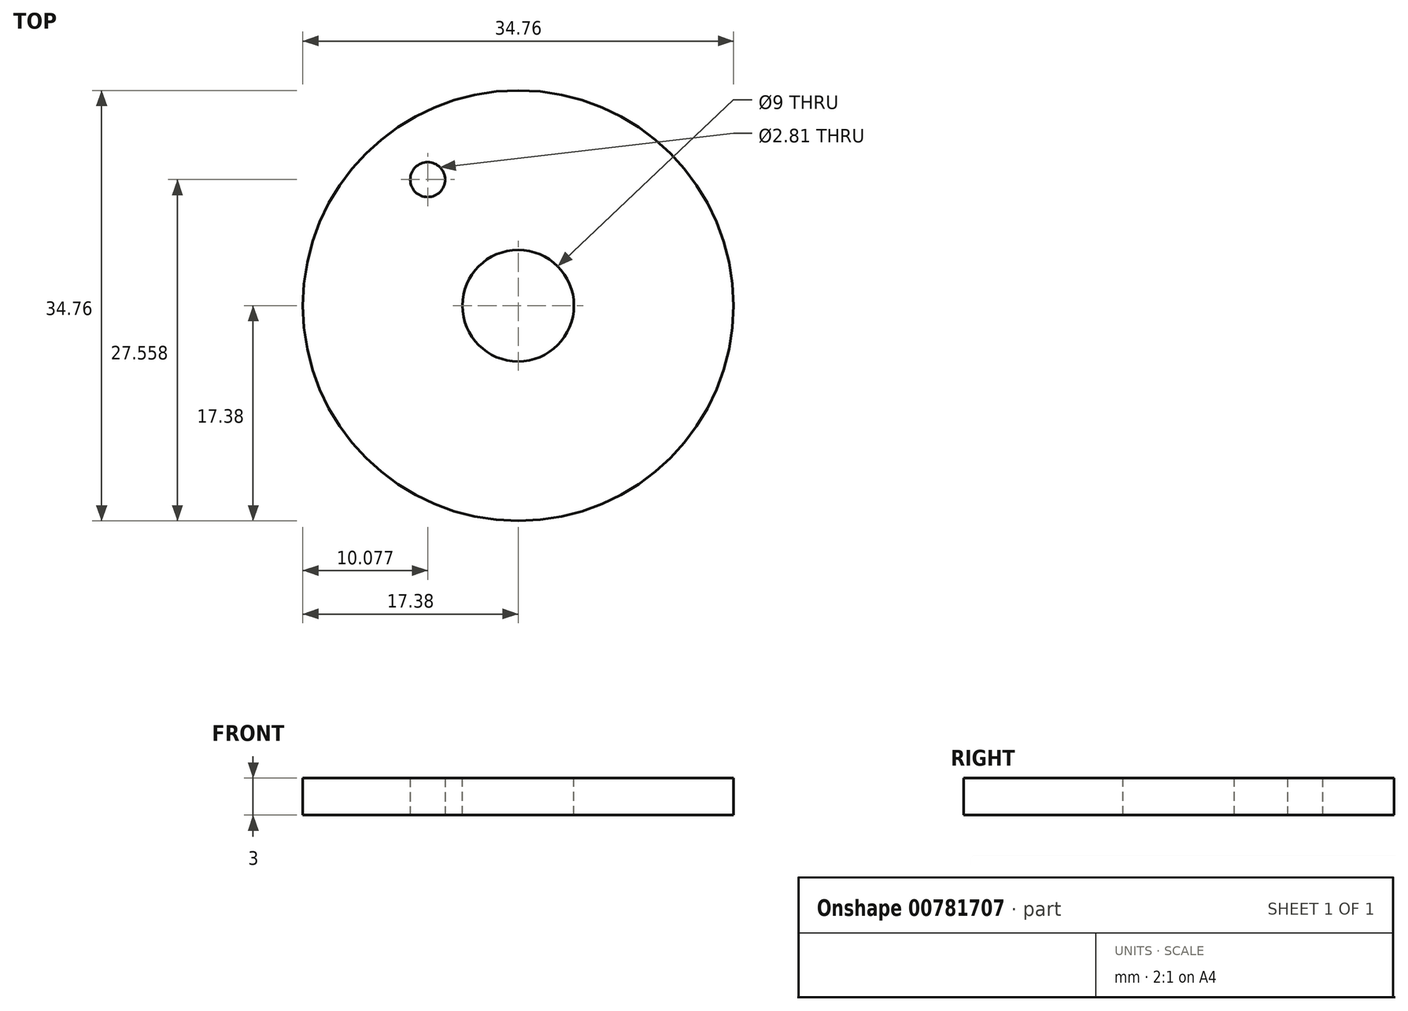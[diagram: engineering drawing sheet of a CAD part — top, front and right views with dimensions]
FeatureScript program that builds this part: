
annotation { "Feature Type Name" : "Feature", "Feature Type Description" : "" }
export const myFeature = defineFeature(function(context is Context, id is Id, definition is map)
    precondition{}
    {
        {
            var Q0;
            Q0=qCreatedBy(makeId("Top.planeOp"),FACE);
            var sketch = newSketch(context, id + "F0", { "sketchPlane" : qUnion([Q0])});
            skCircle(sketch, "E0", {"center": v(0, 0) * mm, "radius": 17.38 * mm});
            skSolve(sketch);
        }
        {
            var Q0;
            Q0=makeQuery(id+"F0.imprint","IMPRINT",FACE,{"disambiguationData":[TD([[makeQuery(id+"F0.imprint","IMPRINT",EDGE,{"derivedFrom":sQuery(id+"F0.wireOp",EDGE,"E0")}),1.0]])]});
            extrude(context, id + "F1", {"entities" : qUnion([Q0]), "depth" : 3 * mm, "offsetDistance" : 25.4 * mm});
        }
        {
            var Q0;
            Q0=makeQuery(id+"F1.opExtrude","CAP_FACE",FACE,{"disambiguationData":[OSD([sQuery(id+"F0.wireOp",EDGE,"E0")])],"isStart":false});
            var sketch = newSketch(context, id + "F2", { "sketchPlane" : qUnion([Q0])});
            skCircle(sketch, "E1", {"center": v(0, 0) * mm, "radius": 4.5 * mm});
            skSolve(sketch);
        }
        {
            var Q0;
            Q0=makeQuery(id+"F2.imprint","IMPRINT",FACE,{"disambiguationData":[TD([[makeQuery(id+"F2.imprint","IMPRINT",EDGE,{"derivedFrom":sQuery(id+"F2.wireOp",EDGE,"E1")}),1.0]])]});
            extrude(context, id + "F3", {"entities" : qUnion([Q0]), "operationType" : NewBodyOperationType.REMOVE, "oppositeDirection" : true, "depth" : 25.4 * mm, "offsetDistance" : 25.4 * mm});
        }
        {
            var Q0;
            Q0=qCreatedBy(makeId("Top.planeOp"),FACE);
            var sketch = newSketch(context, id + "F4", { "sketchPlane" : qUnion([Q0])});
            skCircle(sketch, "E2", {"center": v(-7.3, 10.18) * mm, "radius": 1.4 * mm});
            skSolve(sketch);
        }
        {
            var Q0;
            Q0 = qSketchRegion(id + "F4", true);
            extrude(context, id + "F5", {"entities" : qUnion([Q0]), "operationType" : NewBodyOperationType.REMOVE, "depth" : 25 * mm, "offsetDistance" : 25 * mm});
        }
    });
